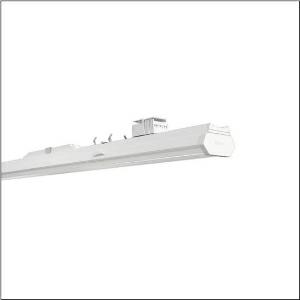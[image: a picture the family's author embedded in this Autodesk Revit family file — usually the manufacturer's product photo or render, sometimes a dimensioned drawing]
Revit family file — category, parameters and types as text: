
# Revit family: licross_21_protected_ho_52td1bmn4exm
name_source: partatom
category: Lighting Fixtures
units: mm (PartAtom-declared; Revit-internal decimal feet)

## family parameters
Cut with Voids When Loaded = No
Host = Face
Light Source = No
Part Type = Normal
Room Calculation Point = No
Round Connector Dimension = Use Diameter
Shared = No

## types (1)
- --- (1 x LED, 14040 lm, 83.2 W, 4000K)
    Apparent Load = 83 VA
    CIE Flux Codes = 54 82 95 97 100
    Color Rendering = 80
    Color Temperature = 4000K
    Default Elevation = 1800 mm
    Description = Licross 21 Protected HO, luminaire insert, of sheet steel, galvanised, coil coated, white, length: 1.500mm, width: 90mm, height: 103mm, LED rated luminous flux: 14.040lm, light colour: 840, SDCM (Standard Deviation of Colour Matching)MacAdam ≤ 3 SDCM (initial), control gear: ON/OFF Multilumen, with plug, 3-pole, with phase selection, mains connection: 220..240V, AC, 50/60Hz, rated input power: 83W, internal wiring halogen-free, primary optical cover: cover, of PMMA, light emission: direct distribution, primary light characteristic: symmetric, protection rating (complete): IP54, insulation class (complete): insulation class I (protective earthing), certification: CE, ENEC, VDE, UKCA, protection symbol: D if used in an environment with non-conductive dust loads with corresponding accessories, impact resistance: IK06, permissible ambient temperature for indoor applications: -35..+35°C, corresponds to IFS (International Featured Standards) requirements for safety and quality in the food industry, reducing of maximum allowable ambient temperature of 5°C with ceiling mounting, LABS conformity tested according to VDMA 24364:2018-05, The light source and the operating device comply with the requirements of the Ecodesign Regulation (EU) 2019/2020 and are replaceable in accordance with this regulation, packaging unit: 1 piece
    Height = 92 mm
    Lamp = 1 x LED
    Lamp Light Flux = 14040 lm
    Lamp Power = 83.2 W
    Lamp count = 1
    Length = 1500 mm
    Luminous efficacy = 169 lm/W
    Manufacturer = Siteco
    ModVariant = No
    Model = 52TD1BMN4EXM
    Mounting Place = Ceiling
    Mounting Type = Pendant
    Number of Poles = 1
    OnlyDefault = Yes
    Power Factor = 1
    Product Name = Licross 21 Protected HO
    Product group = luminaire insert | ceiling pendant
    ProductGroupID = 901
    Protection Class = Protection class I
    Protection Degree = IP 54
    RLX_Detail_Level = 1
    RLX_Emergency_Light_Flux = 0 lm
    RLX_Emergency_Type = 0
    RLX_Emergency_Type_DB = No
    RlxData = <blob elided: 22277 chars, md5=89ef4da6>
    Socket = socket
    Standby Power = 0 W
    System Light Flux = 14040 lm
    System Power = 83 W
    Type Comments = factory setting: luminous flux: 100 % | (A | C | E) | 195 mA
    Type Image = l_1256148.jpg
    URL = http://relux.com
    VarID = @adj_109153
    Voltage = 0 V
    Weight = 0.00 kg
    Width = 88 mm

## geometry (parser evidence)
native form markers: Blend x4, Sweep x10
no freeform markers — native parametric forms only
